# Revit family: QF_EVEREST_EOMH-48-_-35-S_cat
name_source: partatom
category: Specialty Equipment
revit_build: Autodesk Revit 2017 (Build: 20171027_0315(x64)
units: mm (PartAtom-declared; Revit-internal decimal feet)

## family parameters
Always vertical = Yes
Cut with Voids When Loaded = No
Part Type = Normal
Room Calculation Point = No
Round Connector Dimension = Use Diameter
Shared = No
Work Plane-Based = No

## types (1)
- QF_EVEREST_EOMH-48-_-35-S_cat
    Apparent Power = 863 VA
    BTUH = 0.0 Btu/h
    Conn Conduit = Yes
    Conn Plug = NEMA 5-20P
    Cycle = 60 Hz
    Depth = 34 1/4"
    Description = OPEN AIR MERCHANDISERS
    Elec Conn Connection Height = 0"
    Elec Conn RI Height = 0"
    FL Amps = 8 A
    Foodservice Equipment Identifier = Yes
    HP = 3/4
    Height = 46"
    Identify Quantity as Lot = Yes
    Length = 48"
    Manufacturer = EVEREST
    Materials and Finishes = QF_Plastic - White - Smooth
    Max Overcurrent Protection = 0 A
    Min Ckt Ampacity = 0 A
    Model = EOMH-36-B-35-S
    Number of Poles = 1
    Phase = 1
    Refrigerant Type = R290
    Refrigerant Volume = 0.00 kip
    Volts = 115 V
    Watts = 863 W
    Weight in Pounds = 0

## geometry (parser evidence)
native form markers: Sweep x7
no freeform markers — native parametric forms only
